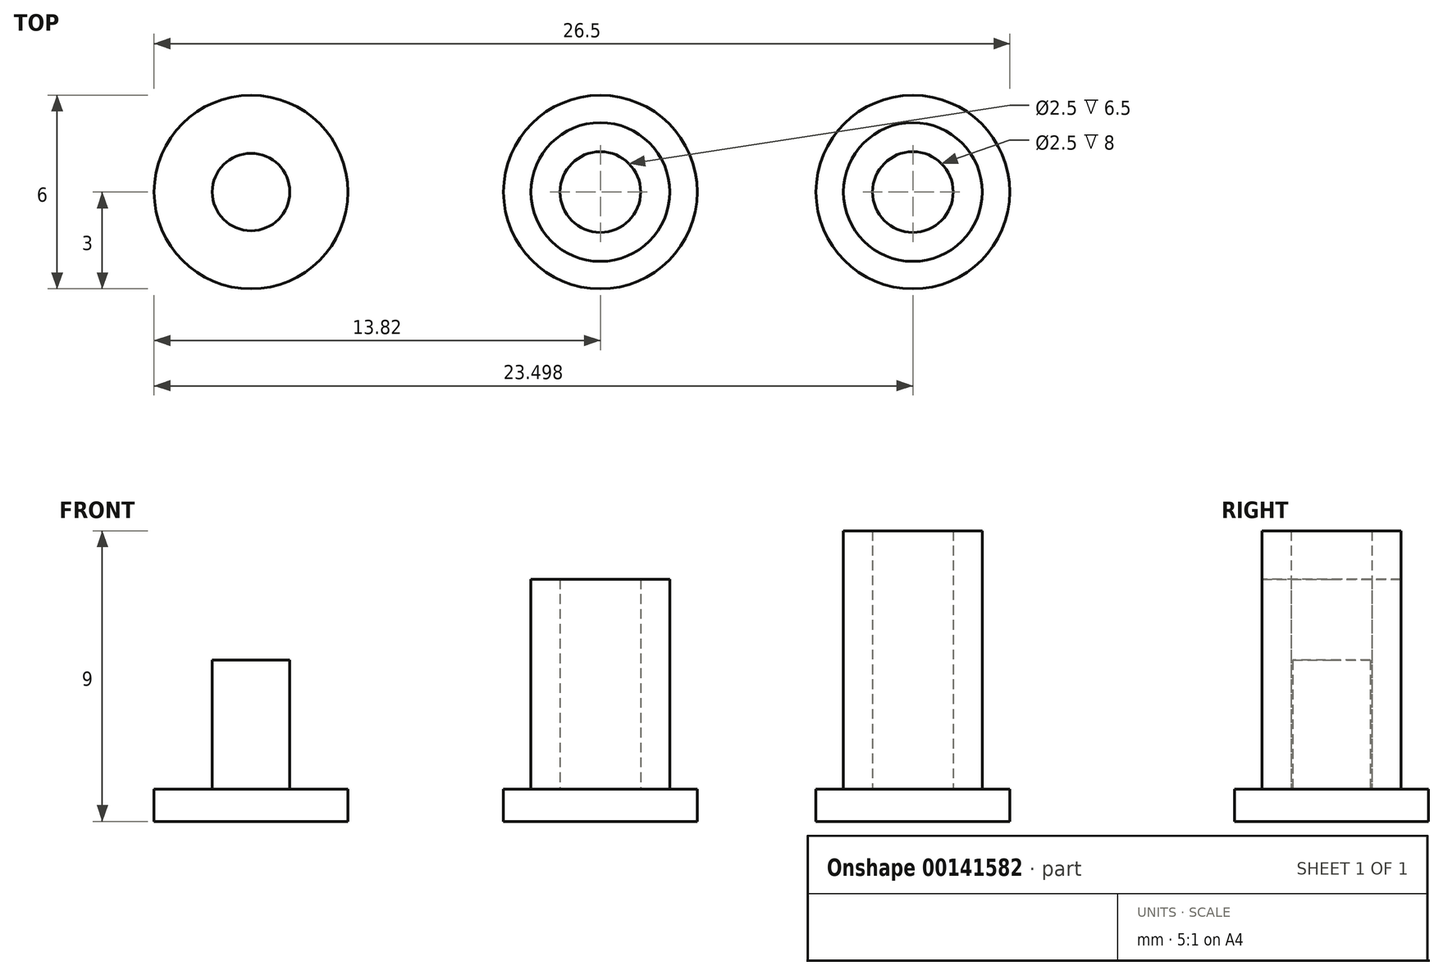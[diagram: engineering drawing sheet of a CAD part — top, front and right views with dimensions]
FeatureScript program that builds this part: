
annotation { "Feature Type Name" : "Feature", "Feature Type Description" : "" }
export const myFeature = defineFeature(function(context is Context, id is Id, definition is map)
    precondition{}
    {
        {
            var Q0;
            Q0=qCreatedBy(makeId("Top.planeOp"),FACE);
            var sketch = newSketch(context, id + "F0", { "sketchPlane" : qUnion([Q0])});
            skCircle(sketch, "E0", {"center": v(0, 0) * mm, "radius": 3 * mm});
            skSolve(sketch);
        }
        {
            var Q0;
            Q0=qSketchRegion(id+"F0",true);
            extrude(context, id + "F1", {"entities" : qUnion([Q0]), "depth" : 1 * mm});
        }
        {
            var Q0;
            Q0=makeQuery(id+"F1.opExtrude","CAP_FACE",FACE,{"disambiguationData":[OSD([sQuery(id+"F0.wireOp",EDGE,"E0")])],"isStart":false});
            var sketch = newSketch(context, id + "F2", { "sketchPlane" : qUnion([Q0])});
            skCircle(sketch, "E1", {"center": v(0, 0) * mm, "radius": 2.15 * mm});
            skCircle(sketch, "E2", {"center": v(0, 0) * mm, "radius": 1.25 * mm});
            skSolve(sketch);
        }
        {
            var Q0;
            Q0=makeQuery(id+"F2.imprint","IMPRINT",FACE,{"disambiguationData":[TD([[makeQuery(id+"F2.imprint","IMPRINT",EDGE,{"derivedFrom":sQuery(id+"F2.wireOp",EDGE,"E1")}),1.0]])]});
            extrude(context, id + "F3", {"entities" : qUnion([Q0]), "operationType" : NewBodyOperationType.ADD, "depth" : 6.5 * mm});
        }
        {
            var Q0;
            Q0=qCreatedBy(makeId("Top.planeOp"),FACE);
            var sketch = newSketch(context, id + "F4", { "sketchPlane" : qUnion([Q0])});
            skCircle(sketch, "E3", {"center": v(-10.82, 0) * mm, "radius": 3 * mm});
            skSolve(sketch);
        }
        {
            var Q0;
            Q0=makeQuery(id+"F4.imprint","IMPRINT",FACE,{"disambiguationData":[TD([[makeQuery(id+"F4.imprint","IMPRINT",EDGE,{"derivedFrom":sQuery(id+"F4.wireOp",EDGE,"E3")}),1.0]])]});
            extrude(context, id + "F5", {"entities" : qUnion([Q0]), "depth" : 1 * mm});
        }
        {
            var Q0;
            Q0=makeQuery(id+"F5.opExtrude","CAP_FACE",FACE,{"disambiguationData":[OSD([sQuery(id+"F4.wireOp",EDGE,"E3")])],"isStart":false});
            var sketch = newSketch(context, id + "F6", { "sketchPlane" : qUnion([Q0])});
            skCircle(sketch, "E4", {"center": v(-10.82, 0) * mm, "radius": 1.2 * mm});
            skSolve(sketch);
        }
        {
            var Q0;
            Q0=makeQuery(id+"F6.imprint","IMPRINT",FACE,{"disambiguationData":[TD([[makeQuery(id+"F6.imprint","IMPRINT",EDGE,{"derivedFrom":sQuery(id+"F6.wireOp",EDGE,"E4")}),1.0]])]});
            extrude(context, id + "F7", {"entities" : qUnion([Q0]), "operationType" : NewBodyOperationType.ADD, "depth" : 4 * mm});
        }
        {
            var Q0;
            Q0=makeQuery(id+"F1.opExtrude","SWEPT_BODY",BODY,{"disambiguationData":[OSD([sQuery(id+"F0.wireOp",EDGE,"E0")])]});
            transform(context, id + "F8", {"entities" : qUnion([Q0]), "transformType" : TransformType.TRANSLATION_3D, "dx" : 9.68 * mm, "dy" : 0 * mm, "dz" : 0 * mm, "makeCopy" : true});
        }
        {
            var Q0;
            Q0=makeQuery(id+"F8.opPattern","COPY",FACE,{"derivedFrom":makeQuery(id+"F3.opExtrude","CAP_FACE",FACE,{"disambiguationData":[OSD([sQuery(id+"F2.wireOp",EDGE,"E1"),sQuery(id+"F2.wireOp",EDGE,"E2")])],"isStart":false}),"instanceName":"1"});
            extrude(context, id + "F9", {"entities" : qUnion([Q0]), "operationType" : NewBodyOperationType.ADD, "depth" : 1.5 * mm});
        }
    });
